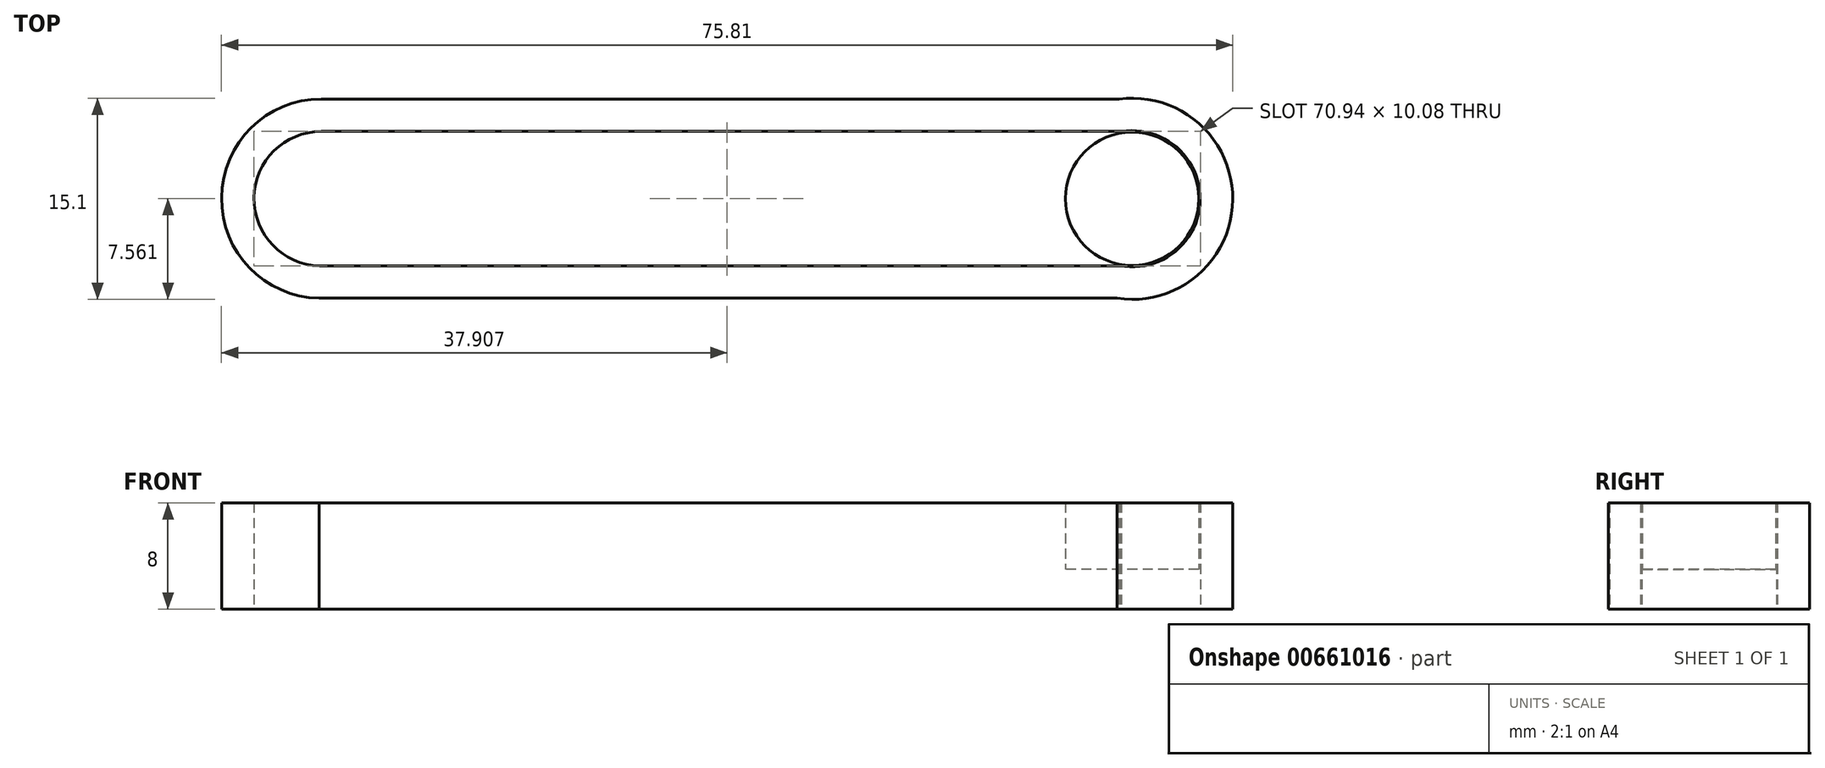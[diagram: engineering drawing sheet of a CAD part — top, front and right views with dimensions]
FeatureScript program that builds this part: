
annotation { "Feature Type Name" : "Feature", "Feature Type Description" : "" }
export const myFeature = defineFeature(function(context is Context, id is Id, definition is map)
    precondition{}
    {
        {
            var Q0;
            Q0=qCreatedBy(makeId("Top.planeOp"),FACE);
            var sketch = newSketch(context, id + "F0", { "sketchPlane" : qUnion([Q0])});
            skArc(sketch, "E0", {"start": v(42.18, -4.92) * mm, "mid": v(48.08, -0.06) * mm, "end": v(42.3, 4.94) * mm});
            skLineSegment(sketch, "E1", {"start": v(42.3, 4.94) * mm, "end": v(-17.7, 4.94) * mm});
            skLineSegment(sketch, "E2", {"start": v(42.18, -4.92) * mm, "end": v(-17.82, -4.92) * mm});
            skArc(sketch, "E3", {"start": v(-17.7, 4.94) * mm, "mid": v(-22.63, 0.07) * mm, "end": v(-17.82, -4.92) * mm});
            skLineSegment(sketch, "E4.0", {"start": v(42.29, 5.05) * mm, "end": v(-17.7, 5.05) * mm});
            skArc(sketch, "E4.1", {"start": v(42.17, -5.03) * mm, "mid": v(48.2, -0.06) * mm, "end": v(42.29, 5.05) * mm});
            skLineSegment(sketch, "E4.2", {"start": v(42.17, -5.03) * mm, "end": v(-17.83, -5.03) * mm});
            skArc(sketch, "E4.3", {"start": v(-17.7, 5.05) * mm, "mid": v(-22.74, 0.07) * mm, "end": v(-17.83, -5.03) * mm});
            skLineSegment(sketch, "E5.0", {"start": v(42.12, 7.48) * mm, "end": v(-17.7, 7.48) * mm});
            skArc(sketch, "E5.1", {"start": v(41.97, -7.46) * mm, "mid": v(50.63, -0.08) * mm, "end": v(42.12, 7.48) * mm});
            skLineSegment(sketch, "E5.2", {"start": v(41.97, -7.46) * mm, "end": v(-17.85, -7.46) * mm});
            skArc(sketch, "E5.3", {"start": v(-17.7, 7.48) * mm, "mid": v(-25.18, 0.08) * mm, "end": v(-17.85, -7.46) * mm});
            skArc(sketch, "E6", {"start": v(-17.7, 5.05) * mm, "mid": v(-12.66, 0.07) * mm, "end": v(-17.58, -5.03) * mm});
            skArc(sketch, "E7", {"start": v(42.3, 4.94) * mm, "mid": v(38.09, 0.06) * mm, "end": v(42.18, -4.92) * mm});
            skSolve(sketch);
        }
        {
            var Q0;
            Q0=makeQuery(id+"F0.imprint","IMPRINT",FACE,{"disambiguationData":[TD([[makeQuery(id+"F0.imprint","IMPRINT",EDGE,{"derivedFrom":sQuery(id+"F0.wireOp",EDGE,"E4.0")}),-1.0]])]});
            var Q1;
            Q1=makeQuery(id+"F0.imprint","IMPRINT",FACE,{"disambiguationData":[TD([[makeQuery(id+"F0.imprint","IMPRINT",EDGE,{"derivedFrom":sQuery(id+"F0.wireOp",EDGE,"E0")}),1.0]])]});
            extrude(context, id + "F1", {"entities" : qUnion([Q0, Q1]), "endBound" : BoundingType.SYMMETRIC, "depth" : 5 * mm, "offsetDistance" : 25 * mm});
        }
        {
            var Q0;
            Q0=makeQuery(id+"F1.opExtrude","CAP_FACE",FACE,{"disambiguationData":[OSD([sQuery(id+"F0.wireOp",EDGE,"E4.0"),sQuery(id+"F0.wireOp",EDGE,"E4.1"),sQuery(id+"F0.wireOp",EDGE,"E4.2"),sQuery(id+"F0.wireOp",EDGE,"E4.3"),sQuery(id+"F0.wireOp",EDGE,"E5.0"),sQuery(id+"F0.wireOp",EDGE,"E5.1"),sQuery(id+"F0.wireOp",EDGE,"E5.2"),sQuery(id+"F0.wireOp",EDGE,"E5.3")])],"isStart":true});
            extrude(context, id + "F2", {"entities" : qUnion([Q0]), "operationType" : NewBodyOperationType.ADD, "endBound" : BoundingType.SYMMETRIC, "depth" : 6 * mm, "offsetDistance" : 25 * mm});
        }
    });
